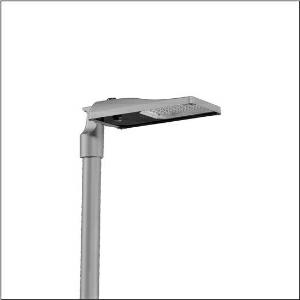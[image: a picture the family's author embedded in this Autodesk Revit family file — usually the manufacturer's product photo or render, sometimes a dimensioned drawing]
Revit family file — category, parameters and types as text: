
# Revit family: streetlight_sl_31_mini___st1_0a_5xh2d31t08ha_99ca
name_source: partatom
category: Lighting Fixtures
units: mm (PartAtom-declared; Revit-internal decimal feet)

## family parameters
Cut with Voids When Loaded = No
Host = Face
Light Source = No
Part Type = Normal
Room Calculation Point = No
Round Connector Dimension = Use Diameter
Shared = No

## types (1)
- --- (1 x LED, 9230 lm, 68.3 W, 3000K)
    Apparent Load = 68 VA
    CIE Flux Codes = 37 72 97 100 100
    Color Rendering = 70
    Color Temperature = 3000K
    Default Elevation = 1800 mm
    Description = Streetlight SL 31 mini D4i, Desk-Remote mast luminaire for post-top, side-entry; light control with lens of PMMA; light distribution: ST1.0a, direct asymmetric distribution, for standard-compliant lighting for roads and squares; LED: luminous flux: 9.230lm, light colour: 730, colour temperature: 3000K; luminous efficacy: 135,1lm/W; control: pre-setting: logarithmic dimming characteristic, flexible luminous flux parameterisation, time-dependent luminous flux control, constant luminous flux control, power reduction, intelligent temperature release in ECG and LED module, overheat protection; luminaire housing, of diecast aluminium, Siteco® metallic grey (DB 702S), corrosivity category C5 high according to DIN EN ISO 12944; cover of toughened safety glass, transparent, mast flange of diecast aluminium, Siteco® metallic grey (DB 702S), spigot size: 76/60mm, mast flange included unmounted; with cable H07RN-F 2x 1.5mm², cable length: 8,5m, connection cable pre-assembled; mains connection: 220..240V, AC, 50/60Hz; power consumption (at start of service life): 68,3W / (at end of service life): 74,5W / (with reduced operation 50%): 29,5W; protection rating (complete): IP66; insulation class (complete): insulation class II (safety insulation); impact resistance: IK09; certification: CE, ENEC, ENEC+, VDE, UKCA, ZD4i; permissible operating ambient temperature for outdoor applications: -40..+50°C; packaging unit: 1 piece

Light Distribution: ST1.0a
    Height = 76 mm
    Lamp = 1 x LED
    Lamp Light Flux = 9230 lm
    Lamp Power = 68.3 W
    Lamp count = 1
    Length = 547 mm
    Luminous efficacy = 135 lm/W
    Manufacturer = Siteco
    ModVariant = No
    Model = 5XH2D31T08HA
    Number of Poles = 1
    OnlyDefault = Yes
    Power Factor = 1
    Product Name = Streetlight SL 31 mini | ST1.0a
    Product group = mast luminaire | pylon top
    ProductGroupID = 6100
    Protection Class = Protection class II
    Protection Degree = IP 66
    RLX_Detail_Level = 1
    RLX_Emergency_Light_Flux = 0 lm
    RLX_Emergency_Type = 0
    RLX_Emergency_Type_DB = No
    RlxData = <blob elided: 24281 chars, md5=06b8bc84>
    Socket = socket
    Standby Power = 0 W
    System Light Flux = 9230 lm
    System Power = 68 W
    Type Comments = factory setting: luminous flux: 100 % | dim-lin: 254 | 692 mA
    Type Image = l_1300332.jpg
    URL = http://relux.com
    VarID = @adj_002249
    Voltage = 0 V
    Weight = 0.00 kg
    Width = 265 mm

## geometry (parser evidence)
native form markers: Blend x4, Sweep x9
no freeform markers — native parametric forms only
